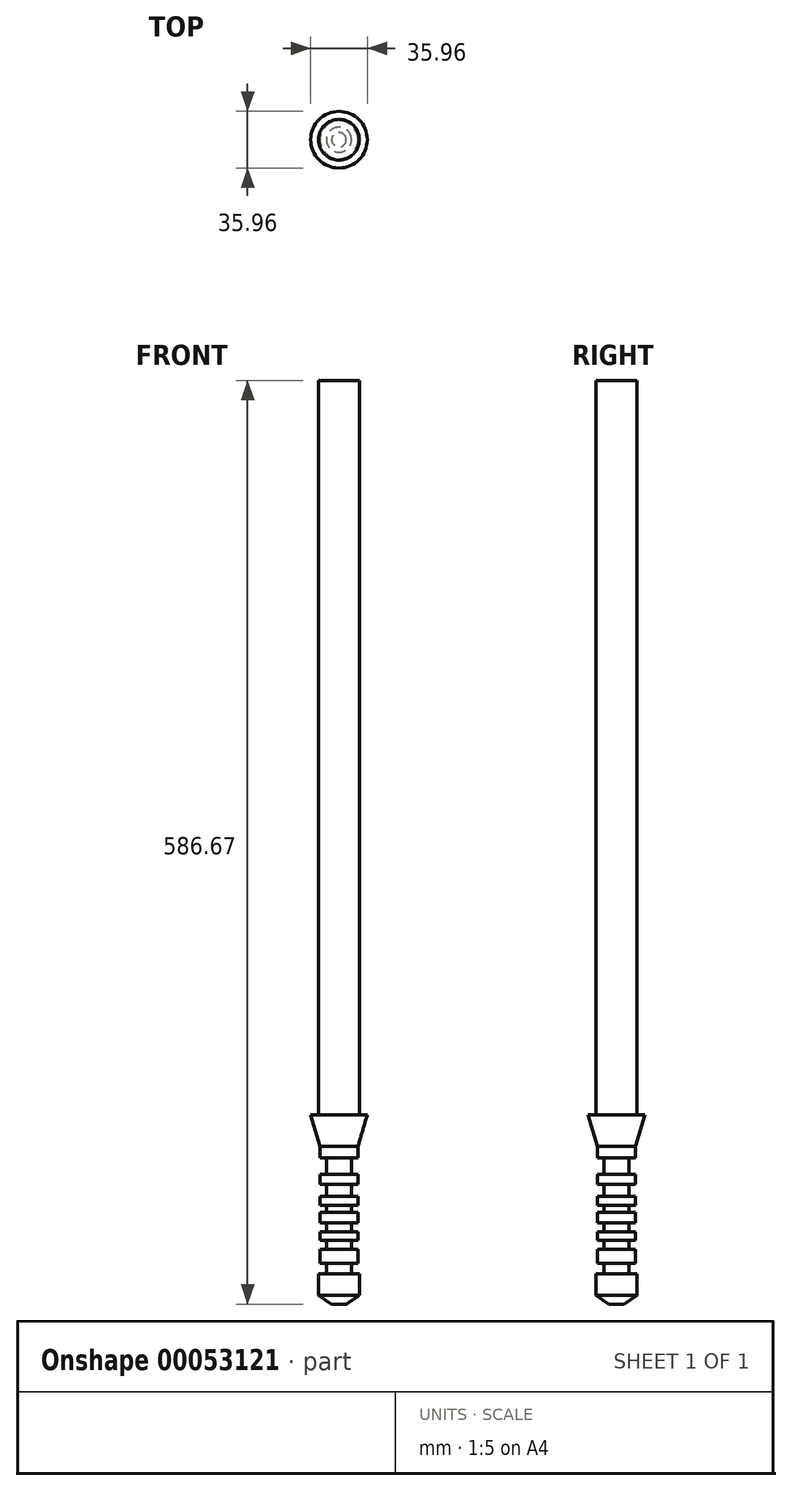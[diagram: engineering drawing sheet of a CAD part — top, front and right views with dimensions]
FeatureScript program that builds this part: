
annotation { "Feature Type Name" : "Feature", "Feature Type Description" : "" }
export const myFeature = defineFeature(function(context is Context, id is Id, definition is map)
    precondition{}
    {
        {
            var Q0;
            Q0=qCreatedBy(makeId("Front.planeOp"),FACE);
            var sketch = newSketch(context, id + "F0", { "sketchPlane" : qUnion([Q0])});
            skLineSegment(sketch, "E0", {"start": v(0, -70.76) * mm, "end": v(4.62, -70.76) * mm});
            skLineSegment(sketch, "E1", {"start": v(13.1, -65.03) * mm, "end": v(4.62, -70.76) * mm});
            skLineSegment(sketch, "E2", {"start": v(13.1, -65.03) * mm, "end": v(13.1, -51.5) * mm});
            skLineSegment(sketch, "E3", {"start": v(13.1, -51.5) * mm, "end": v(7.96, -51.5) * mm});
            skLineSegment(sketch, "E4", {"start": v(7.96, -51.5) * mm, "end": v(7.96, -44.82) * mm});
            skLineSegment(sketch, "E5", {"start": v(7.96, -44.82) * mm, "end": v(12.07, -44.82) * mm});
            skLineSegment(sketch, "E6", {"start": v(12.07, -44.82) * mm, "end": v(12.07, -35.85) * mm});
            skLineSegment(sketch, "E7", {"start": v(12.07, 29.56) * mm, "end": v(17.98, 49.44) * mm});
            skLineSegment(sketch, "E8", {"start": v(17.98, 49.44) * mm, "end": v(0, 49.44) * mm});
            skPoint(sketch, "E9.orphan", {"position": v(0, 37.12) * mm});
            skLineSegment(sketch, "E10", {"start": v(0, 49.44) * mm, "end": v(0, -70.76) * mm});
            skLineSegment(sketch, "E11", {"start": v(7.96, -35.85) * mm, "end": v(7.96, -30.13) * mm});
            skLineSegment(sketch, "E12", {"start": v(7.96, 22.03) * mm, "end": v(12.07, 22.03) * mm});
            skLineSegment(sketch, "E13", {"start": v(7.96, 11.74) * mm, "end": v(12.07, 11.74) * mm});
            skLineSegment(sketch, "E14", {"start": v(7.96, 5.45) * mm, "end": v(12.07, 5.45) * mm});
            skLineSegment(sketch, "E15", {"start": v(7.96, -2.27) * mm, "end": v(12.07, -2.27) * mm});
            skLineSegment(sketch, "E16", {"start": v(7.96, -7.83) * mm, "end": v(12.07, -7.83) * mm});
            skLineSegment(sketch, "E17", {"start": v(7.96, -12.56) * mm, "end": v(12.07, -12.56) * mm});
            skLineSegment(sketch, "E18", {"start": v(7.96, -18.99) * mm, "end": v(12.07, -18.99) * mm});
            skLineSegment(sketch, "E19", {"start": v(7.96, -24.85) * mm, "end": v(12.07, -24.85) * mm});
            skLineSegment(sketch, "E20", {"start": v(7.96, -30.13) * mm, "end": v(12.07, -30.13) * mm});
            skLineSegment(sketch, "E21", {"start": v(7.96, -35.85) * mm, "end": v(12.07, -35.85) * mm});
            skLineSegment(sketch, "E22.trimOffspring", {"start": v(12.07, -30.13) * mm, "end": v(12.07, -24.85) * mm});
            skLineSegment(sketch, "E23.trimOffspring", {"start": v(7.96, -24.85) * mm, "end": v(7.96, -18.99) * mm});
            skLineSegment(sketch, "E24.trimOffspring", {"start": v(12.07, -18.99) * mm, "end": v(12.07, -12.56) * mm});
            skLineSegment(sketch, "E25.trimOffspring", {"start": v(7.96, -12.56) * mm, "end": v(7.96, -7.83) * mm});
            skLineSegment(sketch, "E26.trimOffspring", {"start": v(12.07, -7.83) * mm, "end": v(12.07, -2.27) * mm});
            skLineSegment(sketch, "E27.trimOffspring", {"start": v(7.96, -2.27) * mm, "end": v(7.96, 5.45) * mm});
            skLineSegment(sketch, "E28.trimOffspring", {"start": v(12.07, 5.45) * mm, "end": v(12.07, 11.74) * mm});
            skLineSegment(sketch, "E29.trimOffspring", {"start": v(7.96, 11.74) * mm, "end": v(7.96, 22.03) * mm});
            skLineSegment(sketch, "E30.trimOffspring", {"start": v(12.07, 22.03) * mm, "end": v(12.07, 29.56) * mm});
            skPoint(sketch, "E31.start.orphan", {"position": v(7.96, 29.15) * mm});
            skLineSegment(sketch, "E32", {"start": v(0, 76.84) * mm, "end": v(0, -83.47) * mm});
            skSolve(sketch);
        }
        {
            var Q0;
            Q0 = qSketchRegion(id + "F0", true);
            var Q1;
            Q1=sQuery(id+"F0.wireOp",EDGE,"E32");
            revolve(context, id + "F1", {"entities" : qUnion([Q0]), "axis" : qUnion([Q1]), "revolveType" : RevolveType.FULL});
        }
        {
            var Q0;
            Q0=makeQuery(id+"F1.opRevolve","SWEPT_FACE",FACE,{"disambiguationData":[OSD([sQuery(id+"F0.wireOp",EDGE,"E8")])]});
            var sketch = newSketch(context, id + "F2", { "sketchPlane" : qUnion([Q0])});
            skCircle(sketch, "E33", {"center": v(0, 0) * mm, "radius": 12.92 * mm});
            skSolve(sketch);
        }
        {
            var Q0;
            Q0 = qSketchRegion(id + "F2", true);
            extrude(context, id + "F3", {"entities" : qUnion([Q0]), "operationType" : NewBodyOperationType.ADD, "depth" : 466.47 * mm});
        }
    });
